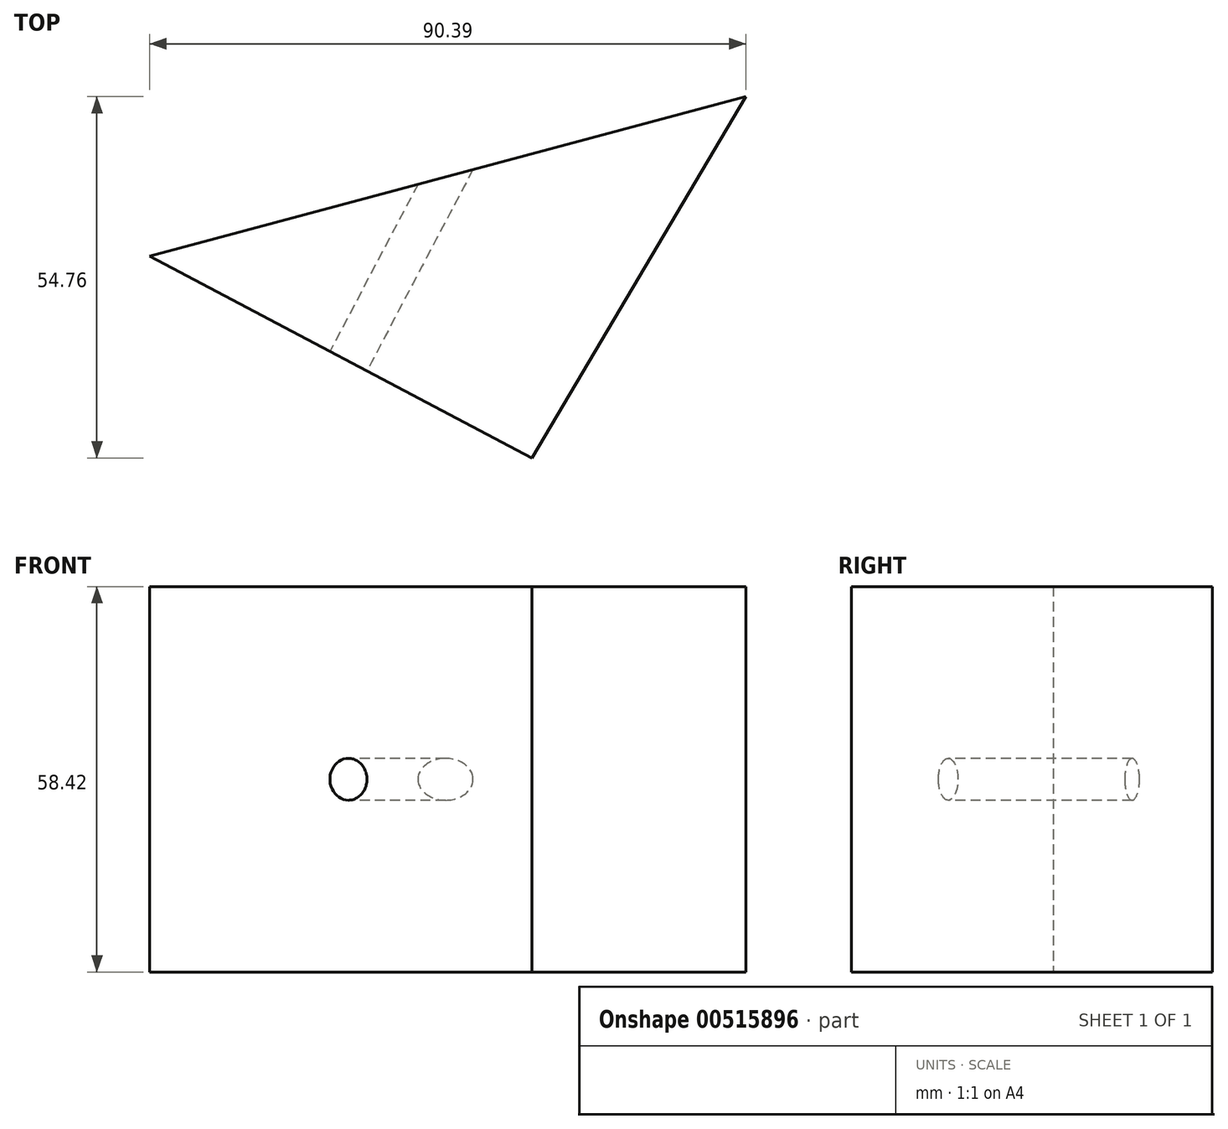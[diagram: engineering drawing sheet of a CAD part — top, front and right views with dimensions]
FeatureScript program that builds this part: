
annotation { "Feature Type Name" : "Feature", "Feature Type Description" : "" }
export const myFeature = defineFeature(function(context is Context, id is Id, definition is map)
    precondition{}
    {
        {
            var Q0;
            Q0=qCreatedBy(makeId("Top.planeOp"),FACE);
            var sketch = newSketch(context, id + "F0", { "sketchPlane" : qUnion([Q0])});
            skLineSegment(sketch, "E0", {"start": v(32.42, 24.17) * mm, "end": v(-57.97, 0) * mm});
            skLineSegment(sketch, "E1", {"start": v(-57.97, 0) * mm, "end": v(0, -30.6) * mm});
            skLineSegment(sketch, "E2", {"start": v(0, -30.6) * mm, "end": v(32.42, 24.17) * mm});
            skSolve(sketch);
        }
        {
            var Q0;
            Q0 = qSketchRegion(id + "F0", true);
            extrude(context, id + "F1", {"entities" : qUnion([Q0]), "depth" : 58.42 * mm, "offsetDistance" : 25.4 * mm});
        }
        {
            var Q0;
            Q0=makeQuery(id+"F1.opExtrude","SWEPT_FACE",FACE,{"disambiguationData":[OSD([sQuery(id+"F0.wireOp",EDGE,"E1")])]});
            var sketch = newSketch(context, id + "F2", { "sketchPlane" : qUnion([Q0])});
            skPoint(sketch, "E3", {"position": v(-17.2, 29.21) * mm});
            skPoint(sketch, "E3.positionSnap0", {"position": v(-51.27, 29.21) * mm});
            skSolve(sketch);
        }
        {
            var Q0;
            Q0=sQuery(id+"F2.wireOp",VERTEX,"E3");
            var Q1;
            Q1=makeQuery(id+"F1.opExtrude","SWEPT_BODY",BODY,{"disambiguationData":[OSD([sQuery(id+"F0.wireOp",EDGE,"E0"),sQuery(id+"F0.wireOp",EDGE,"E1"),sQuery(id+"F0.wireOp",EDGE,"E2")])]});
            hole(context, id + "F3", {"style" : HoleStyle.SIMPLE, "endStyle" : HoleEndStyle.THROUGH, "holeDiameter" : 6.35 * mm, "isTappedThrough" : true, "tappedDepth" : 12.7 * mm, "tapClearance" : 3, "locations" : qUnion([Q0]), "scope" : qUnion([Q1])});
        }
    });
